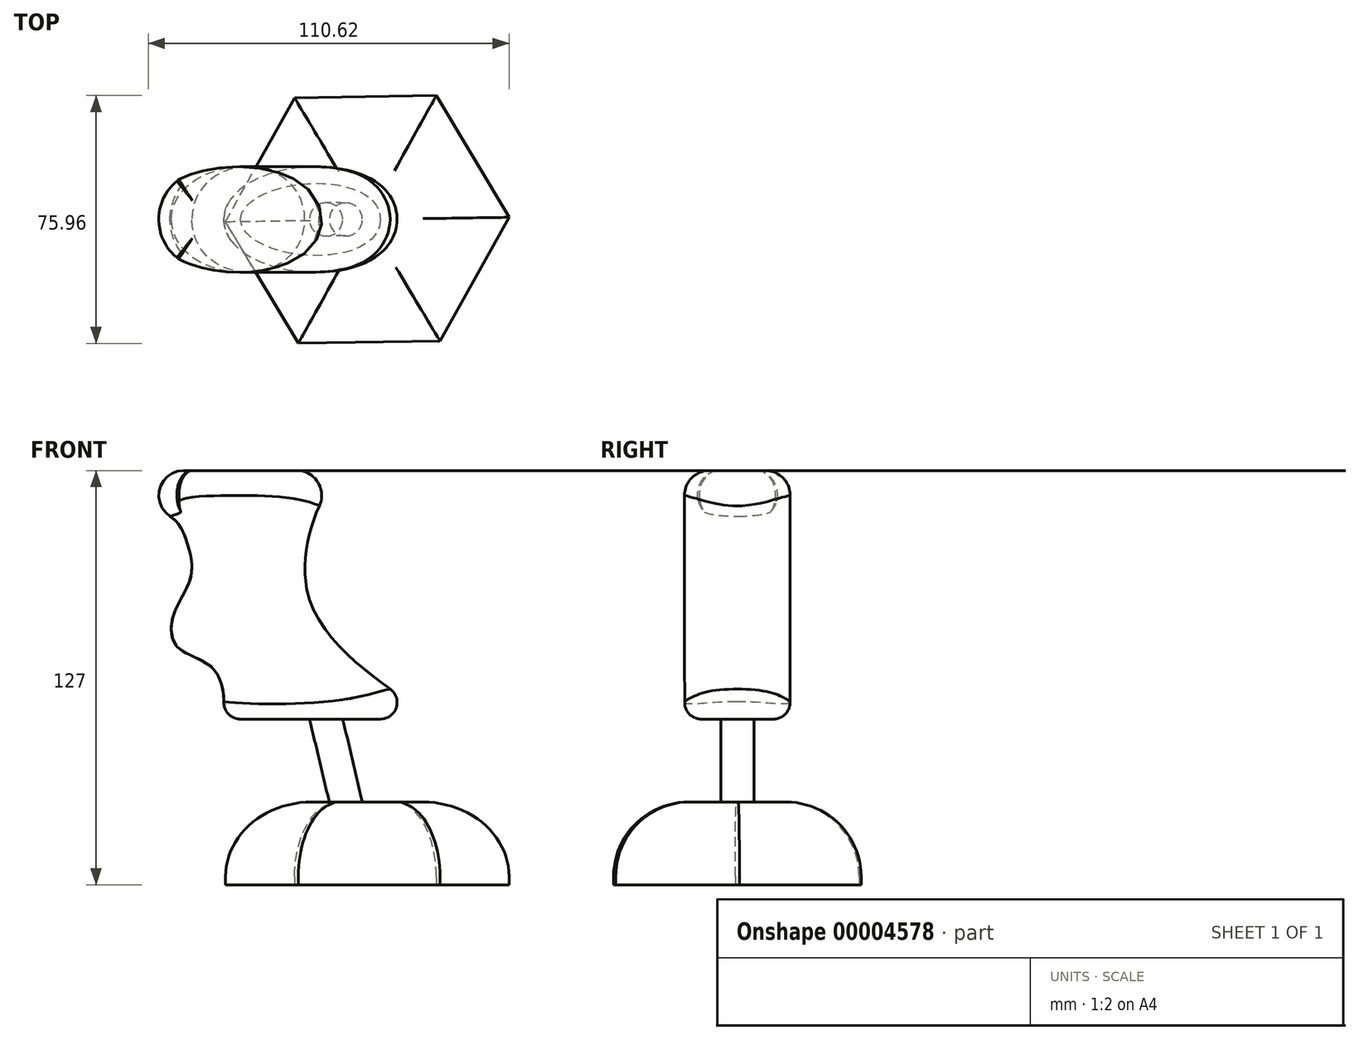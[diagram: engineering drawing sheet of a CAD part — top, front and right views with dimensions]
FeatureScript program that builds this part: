
annotation { "Feature Type Name" : "Feature", "Feature Type Description" : "" }
export const myFeature = defineFeature(function(context is Context, id is Id, definition is map)
    precondition{}
    {
        {
            var Q0;
            Q0=qCreatedBy(makeId("Top.planeOp"),FACE);
            var sketch = newSketch(context, id + "F0", { "sketchPlane" : qUnion([Q0])});
            skEllipse(sketch, "E0", {"center": v(0, 0) * mm, "majorRadius": 33.53 * mm, "minorRadius": 16.14 * mm, "majorAxis": v(1, 0)});
            skSolve(sketch);
        }
        {
            var Q0;
            Q0=qCreatedBy(makeId("Top.planeOp"),FACE);
            cPlane(context, id + "F1", {"entities" : qUnion([Q0]), "cplaneType" : CPlaneType.OFFSET, "offset" : 76.2 * mm, "width" : 152.4 * mm, "height" : 152.4 * mm});
        }
        {
            var Q0;
            Q0=qCreatedBy(id+"F1.planeOp",FACE);
            var sketch = newSketch(context, id + "F2", { "sketchPlane" : qUnion([Q0])});
            skEllipse(sketch, "E1", {"center": v(-24.94, 0) * mm, "majorRadius": 30.07 * mm, "minorRadius": 16.2 * mm, "majorAxis": v(1, 0)});
            skSolve(sketch);
        }
        {
            var Q0;
            Q0=qCreatedBy(makeId("Front.planeOp"),FACE);
            var sketch = newSketch(context, id + "F3", { "sketchPlane" : qUnion([Q0])});
            skFitSpline(sketch, "E2", {"points": [v(-55, 76.2) * mm, v(-53.9, 66.3) * mm, v(-46.84, 61.45) * mm, v(-42.38, 53.27) * mm, v(-41.56, 43.27) * mm, v(-46.8, 31.96) * mm, v(-45.64, 22.15) * mm, v(-35.44, 16.2) * mm, v(-31.35, 6.33) * mm, v(-33.53, 0) * mm], "startDerivative": vector(-14.56, -93.29) * mm, "endDerivative": vector(-53.93, -61.08) * mm});
            skSolve(sketch);
        }
        {
            var Q0;
            Q0=qCreatedBy(makeId("Front.planeOp"),FACE);
            var sketch = newSketch(context, id + "F4", { "sketchPlane" : qUnion([Q0])});
            skFitSpline(sketch, "E3", {"points": [v(5.14, 76.2) * mm, v(-4.77, 58.01) * mm, v(-3.85, 33.45) * mm, v(33.53, 0) * mm], "startDerivative": vector(-54.07, -59.45) * mm, "endDerivative": vector(119.6, -74.59) * mm});
            skSolve(sketch);
        }
        {
            var Q0;
            Q0=makeQuery(id+"F0.imprint","IMPRINT",FACE,{"disambiguationData":[TD([[makeQuery(id+"F0.imprint","IMPRINT",EDGE,{"derivedFrom":sQuery(id+"F0.wireOp",EDGE,"E0")}),1.0]])]});
            var Q1;
            Q1=makeQuery(id+"F2.imprint","IMPRINT",FACE,{"disambiguationData":[TD([[makeQuery(id+"F2.imprint","IMPRINT",EDGE,{"derivedFrom":sQuery(id+"F2.wireOp",EDGE,"E1")}),1.0]])]});
            var Q2;
            Q2=sQuery(id+"F3.wireOp",EDGE,"E2");
            var Q3;
            Q3=sQuery(id+"F4.wireOp",EDGE,"E3");
            loft(context, id + "F5", {"addGuides" : true, "sheetProfilesArray" : [{ "sheetProfileEntities" : qUnion([Q0]) }, { "sheetProfileEntities" : qUnion([Q1]) }], "guidesArray" : [{ "guideEntities" : qUnion([Q2]), "guideDerivativeType" : LoftGuideDerivativeType.DEFAULT, "guideDerivativeMagnitude" : 1 }, { "guideEntities" : qUnion([Q3]), "guideDerivativeType" : LoftGuideDerivativeType.DEFAULT, "guideDerivativeMagnitude" : 1 }]});
        }
        {
            var Q0;
            Q0=makeQuery(id+"F5.opLoft","CAP_FACE",FACE,{"disambiguationData":[OSD([makeQuery(id+"F2.imprint","IMPRINT",FACE,{"disambiguationData":[TD([[makeQuery(id+"F2.imprint","IMPRINT",EDGE,{"derivedFrom":sQuery(id+"F2.wireOp",EDGE,"E1")}),1.0]])]})])],"isStart":true});
            fillet(context, id + "F6", {"entities" : qUnion([Q0]), "radius" : 7.62 * mm, "tangentPropagation" : true, "allowEdgeOverflow" : false});
        }
        {
            var Q0;
            Q0=makeQuery(id+"F5.opLoft","CAP_FACE",FACE,{"disambiguationData":[OSD([makeQuery(id+"F0.imprint","IMPRINT",FACE,{"disambiguationData":[TD([[makeQuery(id+"F0.imprint","IMPRINT",EDGE,{"derivedFrom":sQuery(id+"F0.wireOp",EDGE,"E0")}),1.0]])]})])],"isStart":true});
            var sketch = newSketch(context, id + "F7", { "sketchPlane" : qUnion([Q0])});
            skCircle(sketch, "E4", {"center": v(0, 0) * mm, "radius": 5.1 * mm});
            skSolve(sketch);
        }
        {
            var Q0;
            Q0=qCreatedBy(makeId("Top.planeOp"),FACE);
            cPlane(context, id + "F8", {"entities" : qUnion([Q0]), "cplaneType" : CPlaneType.OFFSET, "offset" : 50.8 * mm, "oppositeDirection" : true, "width" : 152.4 * mm, "height" : 152.4 * mm});
        }
        {
            var Q0;
            Q0=qCreatedBy(id+"F8.planeOp",FACE);
            var sketch = newSketch(context, id + "F9", { "sketchPlane" : qUnion([Q0])});
            skCircle(sketch, "E5", {"center": v(12.05, 0) * mm, "radius": 5.05 * mm});
            skSolve(sketch);
        }
        {
            var Q0;
            Q0=makeQuery(id+"F9.imprint","IMPRINT",FACE,{"disambiguationData":[TD([[makeQuery(id+"F9.imprint","IMPRINT",EDGE,{"derivedFrom":sQuery(id+"F9.wireOp",EDGE,"E5")}),1.0]])]});
            var Q1;
            Q1=makeQuery(id+"F7.imprint","IMPRINT",FACE,{"disambiguationData":[TD([[makeQuery(id+"F7.imprint","IMPRINT",EDGE,{"derivedFrom":sQuery(id+"F7.wireOp",EDGE,"E4")}),1.0]])]});
            loft(context, id + "F10", {"sheetProfilesArray" : [{ "sheetProfileEntities" : qUnion([Q0]) }, { "sheetProfileEntities" : qUnion([Q1]) }]});
        }
        {
            var Q0;
            Q0=makeQuery(id+"F5.opLoft","MID_CAP_EDGE",EDGE,{"disambiguationData":[OSD([sQuery(id+"F0.wireOp",EDGE,"E0"),sQuery(id+"F3.wireOp",EDGE,"E2"),sQuery(id+"F4.wireOp",EDGE,"E3")]),OD(0.0)],"capPos":0.0});
            fillet(context, id + "F11", {"entities" : qUnion([Q0]), "radius" : 5.08 * mm, "tangentPropagation" : true, "allowEdgeOverflow" : false});
        }
        {
            var Q0;
            Q0=qCreatedBy(id+"F8.planeOp",FACE);
            var sketch = newSketch(context, id + "F12", { "sketchPlane" : qUnion([Q0])});
            skCircle(sketch, "E6.cCircle", {"center": v(12.6, 0) * mm, "radius": 37.65 * mm, "construction": true});
            skLineSegment(sketch, "E6.0", {"start": v(33.77, 37.98) * mm, "end": v(56.08, 0.66) * mm});
            skLineSegment(sketch, "E6.1", {"start": v(56.08, 0.66) * mm, "end": v(34.92, -37.31) * mm});
            skLineSegment(sketch, "E6.2", {"start": v(34.92, -37.31) * mm, "end": v(-8.55, -37.98) * mm});
            skLineSegment(sketch, "E6.3", {"start": v(-8.55, -37.98) * mm, "end": v(-30.86, -0.66) * mm});
            skLineSegment(sketch, "E6.4", {"start": v(-30.86, -0.66) * mm, "end": v(-9.7, 37.31) * mm});
            skLineSegment(sketch, "E6.5", {"start": v(-9.7, 37.31) * mm, "end": v(33.77, 37.98) * mm});
            skPoint(sketch, "E6.0.midPoint", {"position": v(44.92, 19.32) * mm});
            skSolve(sketch);
        }
        {
            var Q0;
            Q0 = qSketchRegion(id + "F12", true);
            extrude(context, id + "F13", {"entities" : qUnion([Q0]), "operationType" : NewBodyOperationType.ADD, "depth" : 25.4 * mm});
        }
        {
            var Q0;
            Q0=makeQuery(id+"F13.opExtrude","CAP_EDGE",EDGE,{"disambiguationData":[OSD([sQuery(id+"F12.wireOp",EDGE,"E6.1")])],"isStart":false});
            var Q1;
            Q1=makeQuery(id+"F13.opExtrude","CAP_EDGE",EDGE,{"disambiguationData":[OSD([sQuery(id+"F12.wireOp",EDGE,"E6.2")])],"isStart":false});
            var Q2;
            Q2=makeQuery(id+"F13.opExtrude","CAP_EDGE",EDGE,{"disambiguationData":[OSD([sQuery(id+"F12.wireOp",EDGE,"E6.3")])],"isStart":false});
            var Q3;
            Q3=makeQuery(id+"F13.opExtrude","CAP_EDGE",EDGE,{"disambiguationData":[OSD([sQuery(id+"F12.wireOp",EDGE,"E6.4")])],"isStart":false});
            var Q4;
            Q4=makeQuery(id+"F13.opExtrude","CAP_EDGE",EDGE,{"disambiguationData":[OSD([sQuery(id+"F12.wireOp",EDGE,"E6.5")])],"isStart":false});
            var Q5;
            Q5=makeQuery(id+"F13.opExtrude","CAP_EDGE",EDGE,{"disambiguationData":[OSD([sQuery(id+"F12.wireOp",EDGE,"E6.0")])],"isStart":false});
            fillet(context, id + "F14", {"entities" : qUnion([Q0, Q1, Q2, Q3, Q4, Q5]), "radius" : 22.86 * mm, "tangentPropagation" : true, "allowEdgeOverflow" : false});
        }
    });
